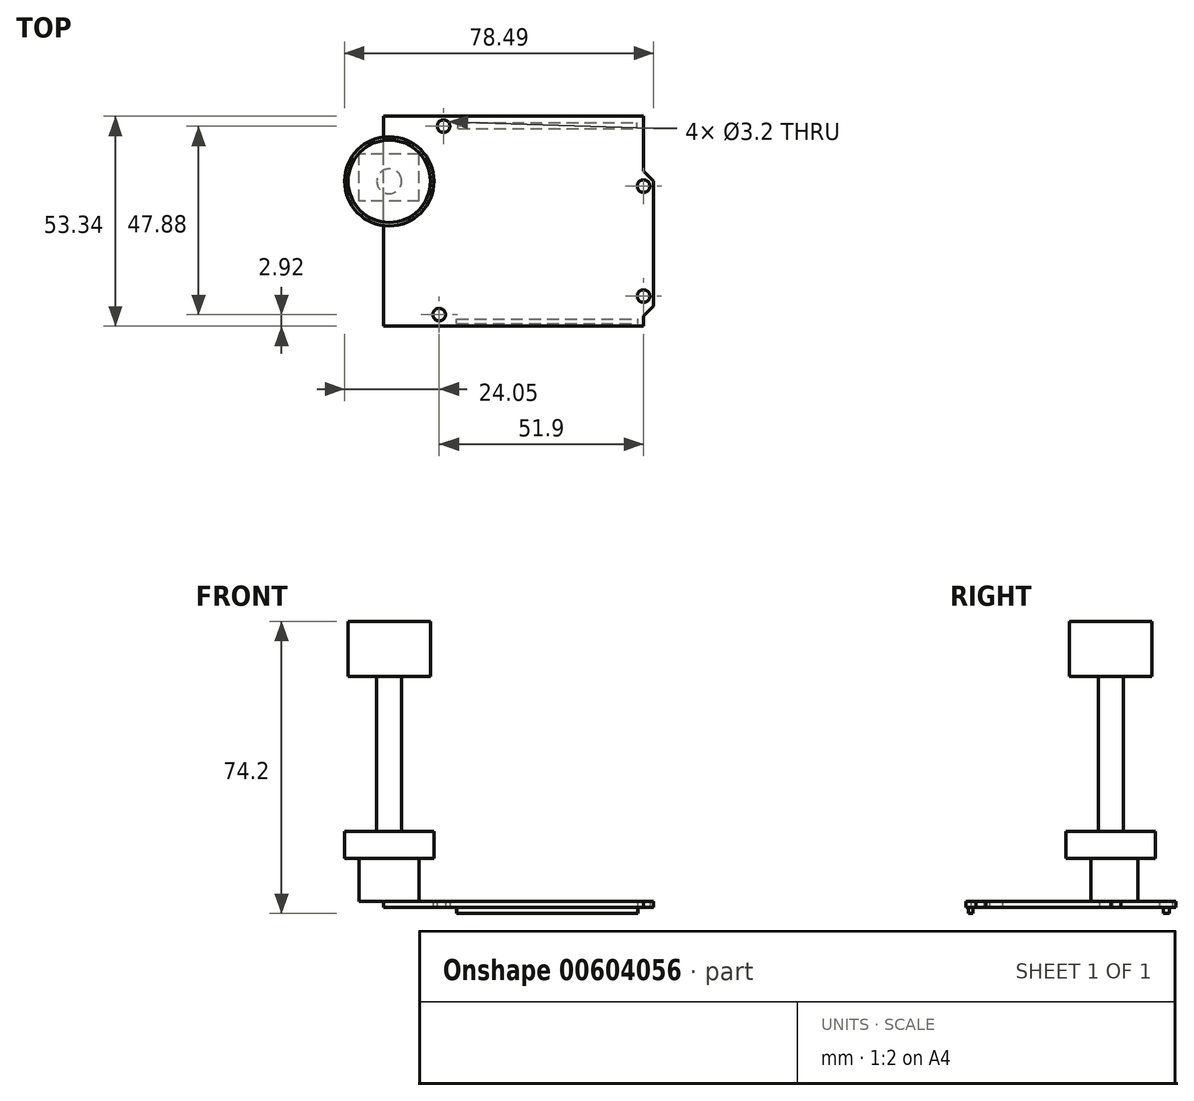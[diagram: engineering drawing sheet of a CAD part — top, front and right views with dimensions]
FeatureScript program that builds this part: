
annotation { "Feature Type Name" : "Feature", "Feature Type Description" : "" }
export const myFeature = defineFeature(function(context is Context, id is Id, definition is map)
    precondition{}
    {
        {
            var Q0;
            Q0=qCreatedBy(makeId("Top.planeOp"),FACE);
            var sketch = newSketch(context, id + "F0", { "sketchPlane" : qUnion([Q0])});
            skLineSegment(sketch, "E0.bottom", {"start": v(0, 0) * mm, "end": v(66.04, 0) * mm});
            skLineSegment(sketch, "E0.top", {"start": v(0, 53.34) * mm, "end": v(66.04, 53.34) * mm});
            skLineSegment(sketch, "E0.left", {"start": v(0, 0) * mm, "end": v(0, 53.34) * mm});
            skLineSegment(sketch, "E0.right", {"start": v(68.58, 5.08) * mm, "end": v(68.58, 36.83) * mm});
            skLineSegment(sketch, "E1", {"start": v(66.04, 0) * mm, "end": v(66.04, 2.54) * mm});
            skLineSegment(sketch, "E2", {"start": v(66.04, 2.54) * mm, "end": v(68.58, 5.08) * mm});
            skLineSegment(sketch, "E3", {"start": v(68.58, 36.83) * mm, "end": v(66.04, 39.37) * mm});
            skLineSegment(sketch, "E4", {"start": v(66.04, 39.37) * mm, "end": v(66.04, 53.34) * mm});
            skCircle(sketch, "E5", {"center": v(66.04, 7.62) * mm, "radius": 1.6 * mm});
            skCircle(sketch, "E6", {"center": v(66.04, 35.56) * mm, "radius": 1.6 * mm});
            skCircle(sketch, "E7", {"center": v(15.24, 50.8) * mm, "radius": 1.6 * mm});
            skPoint(sketch, "E8.orphan", {"position": v(68.58, 0) * mm});
            skCircle(sketch, "E9", {"center": v(14.14, 2.92) * mm, "radius": 1.6 * mm});
            skSolve(sketch);
        }
        {
            var Q0;
            Q0=makeQuery(id+"F0.imprint","IMPRINT",FACE,{"disambiguationData":[TD([[makeQuery(id+"F0.imprint","IMPRINT",EDGE,{"derivedFrom":sQuery(id+"F0.wireOp",EDGE,"E0.bottom")}),1.0]])]});
            extrude(context, id + "F1", {"entities" : qUnion([Q0]), "depth" : 1.6 * mm, "offsetDistance" : 25.4 * mm});
        }
        {
            var Q0;
            Q0=makeQuery(id+"F1.opExtrude","CAP_FACE",FACE,{"disambiguationData":[OSD([sQuery(id+"F0.wireOp",EDGE,"E0.bottom"),sQuery(id+"F0.wireOp",EDGE,"E0.top"),sQuery(id+"F0.wireOp",EDGE,"E0.left"),sQuery(id+"F0.wireOp",EDGE,"E0.right"),sQuery(id+"F0.wireOp",EDGE,"E1"),sQuery(id+"F0.wireOp",EDGE,"E2"),sQuery(id+"F0.wireOp",EDGE,"E3"),sQuery(id+"F0.wireOp",EDGE,"E4"),sQuery(id+"F0.wireOp",EDGE,"E5"),sQuery(id+"F0.wireOp",EDGE,"E6"),sQuery(id+"F0.wireOp",EDGE,"E7")])],"isStart":false});
            var sketch = newSketch(context, id + "F2", { "sketchPlane" : qUnion([Q0])});
            skLineSegment(sketch, "E10.0.0", {"start": v(68.58, 36.83) * mm, "end": v(66.04, 39.37) * mm});
            skLineSegment(sketch, "E10.0.1", {"start": v(66.04, 39.37) * mm, "end": v(66.04, 53.34) * mm});
            skLineSegment(sketch, "E10.0.2", {"start": v(66.04, 53.34) * mm, "end": v(0, 53.34) * mm});
            skLineSegment(sketch, "E10.0.3", {"start": v(0, 53.34) * mm, "end": v(0, 0) * mm});
            skLineSegment(sketch, "E10.0.4", {"start": v(0, 0) * mm, "end": v(66.04, 0) * mm});
            skLineSegment(sketch, "E10.0.5", {"start": v(66.04, 0) * mm, "end": v(66.04, 2.54) * mm});
            skLineSegment(sketch, "E10.0.6", {"start": v(66.04, 2.54) * mm, "end": v(68.58, 5.08) * mm});
            skLineSegment(sketch, "E10.0.7", {"start": v(68.58, 5.08) * mm, "end": v(68.58, 36.83) * mm});
            skLineSegment(sketch, "E11.bottom", {"start": v(9.04, 31.74) * mm, "end": v(-6.2, 31.74) * mm});
            skLineSegment(sketch, "E11.top", {"start": v(9.04, 43.74) * mm, "end": v(-6.2, 43.74) * mm});
            skLineSegment(sketch, "E11.left", {"start": v(9.04, 31.74) * mm, "end": v(9.04, 43.74) * mm});
            skLineSegment(sketch, "E11.right", {"start": v(-6.2, 31.74) * mm, "end": v(-6.2, 43.74) * mm});
            skSolve(sketch);
        }
        {
            var Q0;
            {var subQ5=sQuery(id+"F2.wireOp",EDGE,"E11.right");Q0=makeQuery(id+"F2.imprint","IMPRINT",FACE,{"disambiguationData":[TD([[makeQuery(id+"F2.imprint","IMPRINT",EDGE,{"derivedFrom":subQ5}),-1.0]])]});}
            var Q1;
            {var subQ5=sQuery(id+"F2.wireOp",EDGE,"E11.left");Q1=makeQuery(id+"F2.imprint","IMPRINT",FACE,{"disambiguationData":[TD([[makeQuery(id+"F2.imprint","IMPRINT",EDGE,{"derivedFrom":subQ5}),1.0]])]});}
            extrude(context, id + "F3", {"entities" : qUnion([Q0, Q1]), "operationType" : NewBodyOperationType.ADD, "depth" : 10.9 * mm, "offsetDistance" : 25.4 * mm});
        }
        {
            var Q0;
            Q0=makeQuery(id+"F1.opExtrude","CAP_FACE",FACE,{"disambiguationData":[OSD([sQuery(id+"F0.wireOp",EDGE,"E0.bottom"),sQuery(id+"F0.wireOp",EDGE,"E0.top"),sQuery(id+"F0.wireOp",EDGE,"E0.left"),sQuery(id+"F0.wireOp",EDGE,"E0.right"),sQuery(id+"F0.wireOp",EDGE,"E1"),sQuery(id+"F0.wireOp",EDGE,"E2"),sQuery(id+"F0.wireOp",EDGE,"E3"),sQuery(id+"F0.wireOp",EDGE,"E4"),sQuery(id+"F0.wireOp",EDGE,"E5"),sQuery(id+"F0.wireOp",EDGE,"E6"),sQuery(id+"F0.wireOp",EDGE,"E7"),sQuery(id+"F0.wireOp",EDGE,"E9")])],"isStart":true});
            var sketch = newSketch(context, id + "F4", { "sketchPlane" : qUnion([Q0])});
            skLineSegment(sketch, "E12.bottom", {"start": v(18.54, -0.64) * mm, "end": v(64.63, -0.64) * mm});
            skLineSegment(sketch, "E12.top", {"start": v(18.54, -1.8) * mm, "end": v(64.63, -1.8) * mm});
            skLineSegment(sketch, "E12.left", {"start": v(18.54, -0.64) * mm, "end": v(18.54, -1.8) * mm});
            skLineSegment(sketch, "E12.right", {"start": v(64.63, -0.64) * mm, "end": v(64.63, -1.8) * mm});
            skLineSegment(sketch, "E13.bottom", {"start": v(18.9, -50.17) * mm, "end": v(64.33, -50.17) * mm});
            skLineSegment(sketch, "E13.top", {"start": v(18.9, -51.65) * mm, "end": v(64.33, -51.65) * mm});
            skLineSegment(sketch, "E13.left", {"start": v(18.9, -50.17) * mm, "end": v(18.9, -51.65) * mm});
            skLineSegment(sketch, "E13.right", {"start": v(64.33, -50.17) * mm, "end": v(64.33, -51.65) * mm});
            skSolve(sketch);
        }
        {
            var Q0;
            Q0=makeQuery(id+"F4.imprint","IMPRINT",FACE,{"disambiguationData":[TD([[makeQuery(id+"F4.imprint","IMPRINT",EDGE,{"derivedFrom":sQuery(id+"F4.wireOp",EDGE,"E12.bottom")}),-1.0]])]});
            var Q1;
            Q1=makeQuery(id+"F4.imprint","IMPRINT",FACE,{"disambiguationData":[TD([[makeQuery(id+"F4.imprint","IMPRINT",EDGE,{"derivedFrom":sQuery(id+"F4.wireOp",EDGE,"E13.bottom")}),-1.0]])]});
            extrude(context, id + "F5", {"entities" : qUnion([Q0, Q1]), "operationType" : NewBodyOperationType.ADD, "depth" : 1.5 * mm, "offsetDistance" : 25.4 * mm});
        }
        {
            var Q0;
            Q0=makeQuery(id+"F3.opExtrude","CAP_FACE",FACE,{"disambiguationData":[OSD([sQuery(id+"F2.wireOp",EDGE,"E11.bottom"),sQuery(id+"F2.wireOp",EDGE,"E11.top"),sQuery(id+"F2.wireOp",EDGE,"E11.left"),sQuery(id+"F2.wireOp",EDGE,"E11.right")])],"isStart":false});
            var sketch = newSketch(context, id + "F6", { "sketchPlane" : qUnion([Q0])});
            skCircle(sketch, "E14", {"center": v(1.44, 36.8) * mm, "radius": 3.23 * mm});
            skCircle(sketch, "E15", {"center": v(1.44, 36.8) * mm, "radius": 11.35 * mm});
            skSolve(sketch);
        }
        {
            var Q0;
            Q0=makeQuery(id+"F6.imprint","IMPRINT",FACE,{"disambiguationData":[TD([[makeQuery(id+"F6.imprint","IMPRINT",EDGE,{"derivedFrom":sQuery(id+"F6.wireOp",EDGE,"E15")}),1.0]])]});
            var Q1;
            Q1=makeQuery(id+"F6.imprint","IMPRINT",FACE,{"disambiguationData":[TD([[makeQuery(id+"F6.imprint","IMPRINT",EDGE,{"derivedFrom":sQuery(id+"F6.wireOp",EDGE,"E14")}),-1.0]])]});
            var Q2;
            Q2=makeQuery(id+"F6.imprint","IMPRINT",FACE,{"disambiguationData":[TD([[makeQuery(id+"F6.imprint","IMPRINT",EDGE,{"derivedFrom":sQuery(id+"F6.wireOp",EDGE,"E14")}),1.0]])]});
            extrude(context, id + "F7", {"entities" : qUnion([Q0, Q1, Q2]), "operationType" : NewBodyOperationType.ADD, "depth" : 6.86 * mm, "offsetDistance" : 25.4 * mm});
        }
        {
            var Q0;
            Q0=makeQuery(id+"F7.opExtrude","CAP_FACE",FACE,{"disambiguationData":[OSD([sQuery(id+"F6.wireOp",EDGE,"E15")])],"isStart":false});
            var sketch = newSketch(context, id + "F8", { "sketchPlane" : qUnion([Q0])});
            skCircle(sketch, "E16.0.0", {"center": v(1.44, 36.8) * mm, "radius": 11.35 * mm});
            skCircle(sketch, "E17", {"center": v(1.44, 36.8) * mm, "radius": 3.18 * mm});
            skSolve(sketch);
        }
        {
            var Q0;
            Q0=makeQuery(id+"F8.imprint","IMPRINT",FACE,{"disambiguationData":[TD([[makeQuery(id+"F8.imprint","IMPRINT",EDGE,{"derivedFrom":sQuery(id+"F8.wireOp",EDGE,"E17")}),1.0]])]});
            extrude(context, id + "F9", {"entities" : qUnion([Q0]), "operationType" : NewBodyOperationType.ADD, "depth" : 39.37 * mm, "offsetDistance" : 25.4 * mm});
        }
        {
            var Q0;
            Q0=makeQuery(id+"F9.opExtrude","CAP_FACE",FACE,{"disambiguationData":[OSD([sQuery(id+"F8.wireOp",EDGE,"E17")])],"isStart":false});
            var sketch = newSketch(context, id + "F10", { "sketchPlane" : qUnion([Q0])});
            skCircle(sketch, "E18", {"center": v(1.44, 36.8) * mm, "radius": 10.47 * mm});
            skSolve(sketch);
        }
        {
            var Q0;
            Q0=makeQuery(id+"F10.imprint","IMPRINT",FACE,{"disambiguationData":[TD([[makeQuery(id+"F10.imprint","IMPRINT",EDGE,{"derivedFrom":sQuery(id+"F10.wireOp",EDGE,"E18")}),1.0]])]});
            var Q1;
            Q1=makeQuery(id+"F10.imprint","IMPRINT",FACE,{"disambiguationData":[TD([[makeQuery(id+"F10.imprint","IMPRINT",EDGE,{"derivedFrom":makeQuery(id+"F9.opExtrude","CAP_EDGE",EDGE,{"disambiguationData":[OSD([sQuery(id+"F8.wireOp",EDGE,"E17")])],"isStart":false})}),1.0]])]});
            extrude(context, id + "F11", {"entities" : qUnion([Q0, Q1]), "operationType" : NewBodyOperationType.ADD, "depth" : 13.97 * mm, "offsetDistance" : 25.4 * mm});
        }
    });
